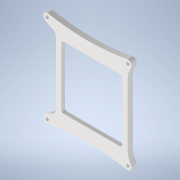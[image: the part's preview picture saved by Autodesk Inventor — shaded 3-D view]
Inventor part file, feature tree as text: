
AUTODESK INVENTOR PART (.ipt)
format: ipt  version: 2021.3 (Build 253353010, 353A)  size: 234,496 bytes
history: native  units: mm
features: reference x9, other x4, extrude x2, sketch x2, projected_geometry x1
ambient origin geometry x8: Origin, YZ Plane, XZ Plane, XY Plane, X Axis, Y Axis, Z Axis, Center Point
bodies: Volumenkörper1 (feature_tree)
feature tree (18):
  extrude  "Extrusion1"  Depth=5.0mm
  extrude  "Extrusion2"  Depth=5.0mm
  sketch  "Skizze1"  dims[d28=5.0mm d29=0.0mm d30=0.5mm]
  reference  "Referenz1"
  reference  "Referenz2"
  reference  "Referenz3"
  reference  "Referenz4"
  reference  "Referenz5"
  sketch  "Skizze2"  dims[d31=2.0mm d32=0.0mm d34=5.0mm d35=5.0mm d36=10.0mm d37=10.0mm d38=3.0mm d39=2.5mm d40=2.5mm d41=45.0deg d42=45.0deg d43=0.25mm d44=0.25mm d45=0.25mm d46=0.25mm d33=0.5mm]
  projected_geometry  "Projizierte Kontur1"
  reference  "Referenz6"
  reference  "Referenz7"
  reference  "Referenz8"
  reference  "Referenz9"
  other  "<userpath>\Documents\Inventor\Scoomatic-Jetson\scoomatic_halterung_bg.iam"
  other  "scoomatic_halterung_bg.iam"
  other  "jetson_dummy:1"
  other  "Bauteil2:1"
